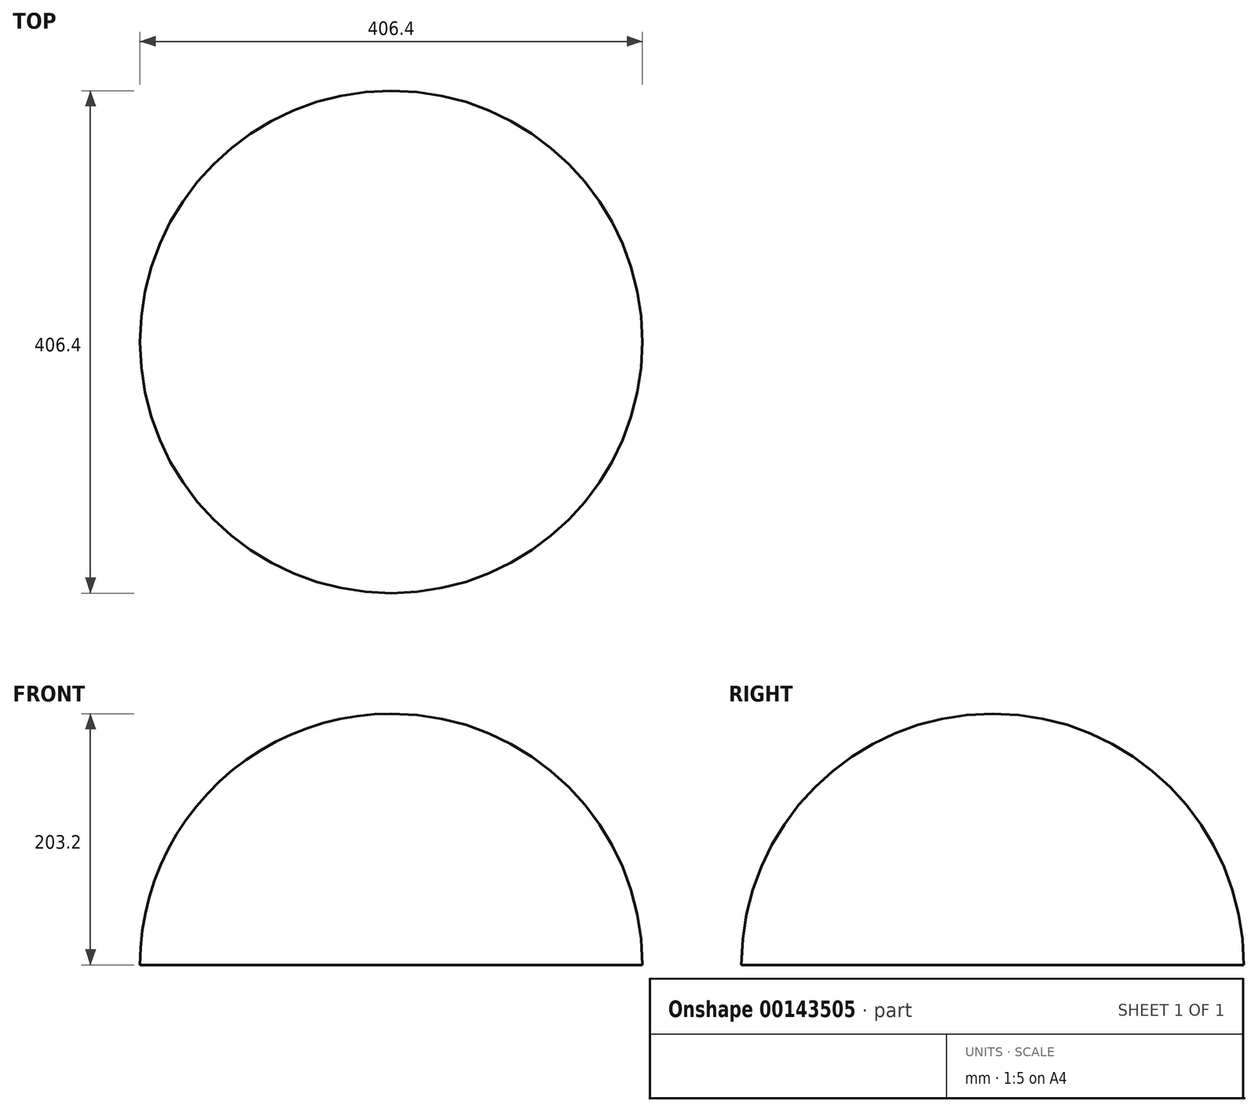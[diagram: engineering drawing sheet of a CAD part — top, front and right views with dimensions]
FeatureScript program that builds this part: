
annotation { "Feature Type Name" : "Feature", "Feature Type Description" : "" }
export const myFeature = defineFeature(function(context is Context, id is Id, definition is map)
    precondition{}
    {
        {
            var Q0;
            Q0=qCreatedBy(makeId("Front.planeOp"),FACE);
            var sketch = newSketch(context, id + "F0", { "sketchPlane" : qUnion([Q0])});
            skArc(sketch, "E0", {"start": v(-203.2, 0) * mm, "mid": v(0, 203.2) * mm, "end": v(203.2, 0) * mm});
            skLineSegment(sketch, "E1", {"start": v(203.2, 0) * mm, "end": v(-203.2, 0) * mm});
            skLineSegment(sketch, "E2", {"start": v(0, 203.2) * mm, "end": v(0, 0) * mm});
            skSolve(sketch);
        }
        {
            var Q0;
            {var subQ3=sQuery(id+"F0.wireOp",EDGE,"E2");Q0=makeQuery(id+"F0.imprint","IMPRINT",FACE,{"disambiguationData":[TD([[makeQuery(id+"F0.imprint","IMPRINT",EDGE,{"derivedFrom":subQ3}),-1.0]])]});}
            var Q1;
            Q1=sQuery(id+"F0.wireOp",EDGE,"E2");
            revolve(context, id + "F1", {"entities" : qUnion([Q0]), "axis" : qUnion([Q1]), "revolveType" : RevolveType.FULL});
        }
    });
